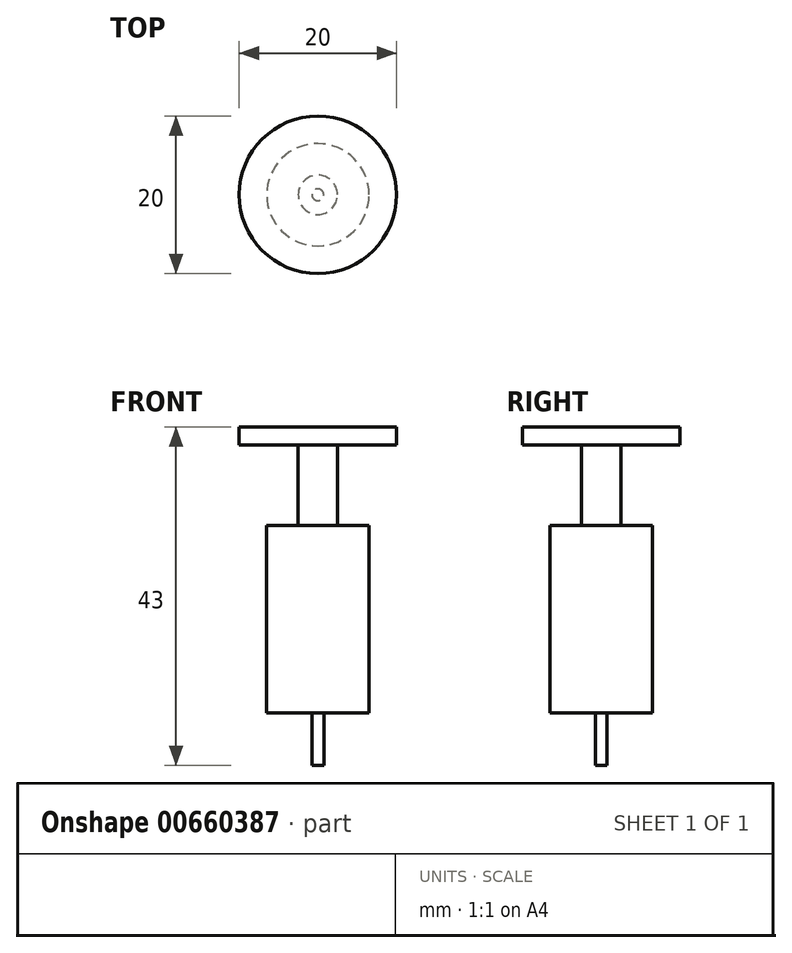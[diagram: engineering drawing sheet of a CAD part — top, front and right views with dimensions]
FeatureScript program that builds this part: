
annotation { "Feature Type Name" : "Feature", "Feature Type Description" : "" }
export const myFeature = defineFeature(function(context is Context, id is Id, definition is map)
    precondition{}
    {
        {
            var Q0;
            Q0=qCreatedBy(makeId("Front.planeOp"),FACE);
            var sketch = newSketch(context, id + "F0", { "sketchPlane" : qUnion([Q0])});
            skLineSegment(sketch, "E0.bottom", {"start": v(-10, 2.3) * mm, "end": v(10, 2.3) * mm});
            skLineSegment(sketch, "E0.top", {"start": v(-10, 0) * mm, "end": v(10, 0) * mm});
            skLineSegment(sketch, "E0.left", {"start": v(-10, 2.3) * mm, "end": v(-10, 0) * mm});
            skLineSegment(sketch, "E0.right", {"start": v(10, 2.3) * mm, "end": v(10, 0) * mm});
            skLineSegment(sketch, "E1.bottom", {"start": v(-2.5, 0) * mm, "end": v(2.5, 0) * mm});
            skLineSegment(sketch, "E1.top", {"start": v(-2.5, -10.2) * mm, "end": v(2.5, -10.2) * mm});
            skLineSegment(sketch, "E1.left", {"start": v(-2.5, 0) * mm, "end": v(-2.5, -10.2) * mm});
            skLineSegment(sketch, "E1.right", {"start": v(2.5, 0) * mm, "end": v(2.5, -10.2) * mm});
            skLineSegment(sketch, "E2.bottom", {"start": v(-6.5, -10.2) * mm, "end": v(6.5, -10.2) * mm});
            skLineSegment(sketch, "E2.top", {"start": v(-6.5, -34) * mm, "end": v(6.5, -34) * mm});
            skLineSegment(sketch, "E2.left", {"start": v(-6.5, -10.2) * mm, "end": v(-6.5, -34) * mm});
            skLineSegment(sketch, "E2.right", {"start": v(6.5, -10.2) * mm, "end": v(6.5, -34) * mm});
            skLineSegment(sketch, "E3.bottom", {"start": v(-0.75, -34) * mm, "end": v(0.75, -34) * mm});
            skLineSegment(sketch, "E3.top", {"start": v(-0.75, -40.7) * mm, "end": v(0.75, -40.7) * mm});
            skLineSegment(sketch, "E3.left", {"start": v(-0.75, -34) * mm, "end": v(-0.75, -40.7) * mm});
            skLineSegment(sketch, "E3.right", {"start": v(0.75, -34) * mm, "end": v(0.75, -40.7) * mm});
            skLineSegment(sketch, "E4", {"start": v(0, 11.44) * mm, "end": v(0, -56.6) * mm});
            skPoint(sketch, "E5", {"position": v(0, 2.3) * mm});
            skPoint(sketch, "E6", {"position": v(0, -10.2) * mm});
            skPoint(sketch, "E7", {"position": v(0, -34) * mm});
            skPoint(sketch, "E8", {"position": v(0, -40.7) * mm});
            skSolve(sketch);
        }
        {
            var Q0;
            {var subQ0=sQuery(id+"F0.wireOp",EDGE,"E2.left");Q0=makeQuery(id+"F0.imprint","IMPRINT",FACE,{"disambiguationData":[TD([[makeQuery(id+"F0.imprint","IMPRINT",EDGE,{"derivedFrom":subQ0}),1.0]])]});}
            var Q1;
            {var subQ0=sQuery(id+"F0.wireOp",EDGE,"E1.left");Q1=makeQuery(id+"F0.imprint","IMPRINT",FACE,{"disambiguationData":[TD([[makeQuery(id+"F0.imprint","IMPRINT",EDGE,{"derivedFrom":subQ0}),1.0]])]});}
            var Q2;
            {var subQ5=sQuery(id+"F0.wireOp",EDGE,"E0.left");Q2=makeQuery(id+"F0.imprint","IMPRINT",FACE,{"disambiguationData":[TD([[makeQuery(id+"F0.imprint","IMPRINT",EDGE,{"derivedFrom":subQ5}),1.0]])]});}
            var Q3;
            {var subQ0=sQuery(id+"F0.wireOp",EDGE,"E3.left");Q3=makeQuery(id+"F0.imprint","IMPRINT",FACE,{"disambiguationData":[TD([[makeQuery(id+"F0.imprint","IMPRINT",EDGE,{"derivedFrom":subQ0}),1.0]])]});}
            var Q4;
            Q4=sQuery(id+"F0.wireOp",EDGE,"E4");
            revolve(context, id + "F1", {"entities" : qUnion([Q0, Q1, Q2, Q3]), "axis" : qUnion([Q4]), "revolveType" : RevolveType.FULL});
        }
    });
